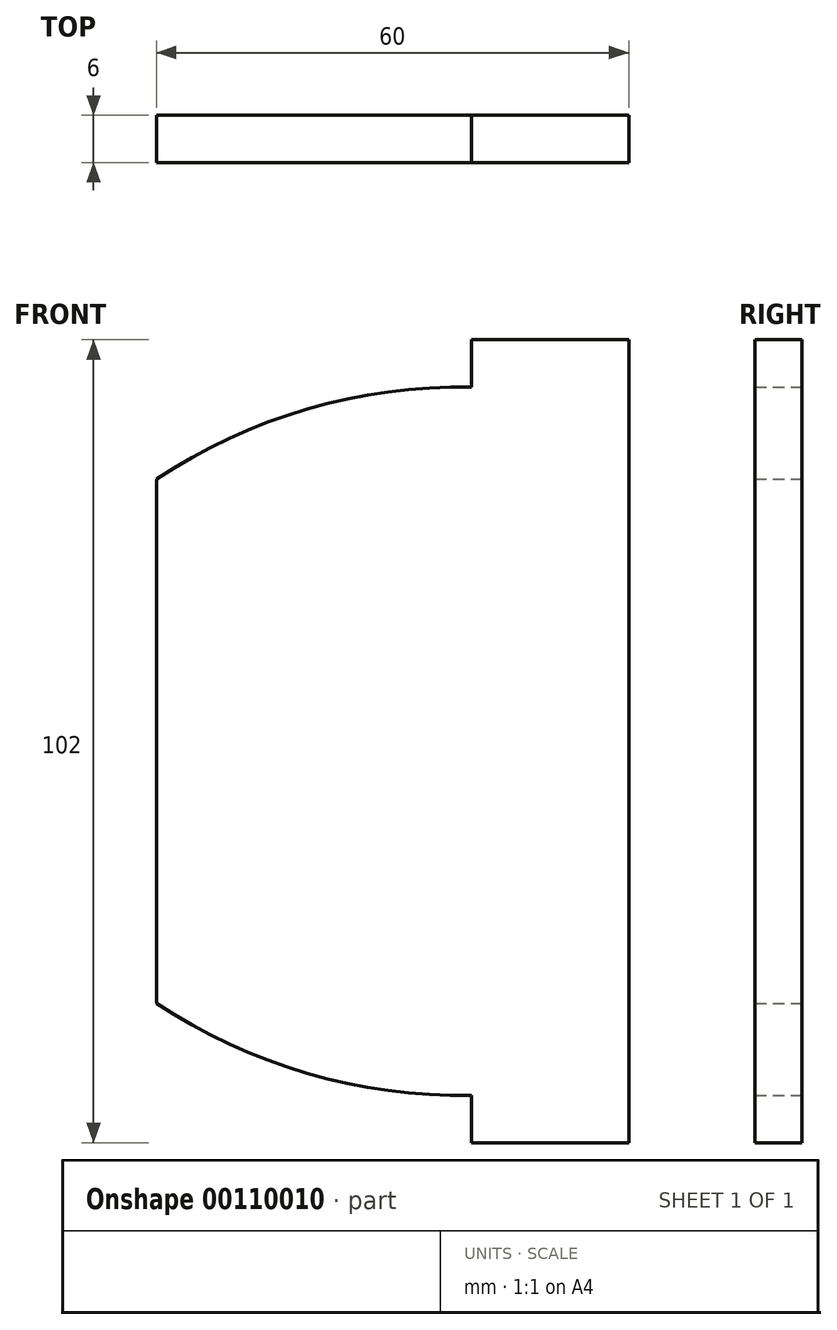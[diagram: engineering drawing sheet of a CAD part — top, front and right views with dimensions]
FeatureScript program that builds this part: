
annotation { "Feature Type Name" : "Feature", "Feature Type Description" : "" }
export const myFeature = defineFeature(function(context is Context, id is Id, definition is map)
    precondition{}
    {
        {
            var Q0;
            Q0=qCreatedBy(makeId("Front.planeOp"),FACE);
            var sketch = newSketch(context, id + "F0", { "sketchPlane" : qUnion([Q0])});
            skLineSegment(sketch, "E0.right", {"start": v(-45, -33.3) * mm, "end": v(-45, 33.3) * mm});
            skPoint(sketch, "E0.middle", {"position": v(0, 0) * mm});
            skLineSegment(sketch, "E1.top", {"start": v(-5, 51) * mm, "end": v(15, 51) * mm});
            skLineSegment(sketch, "E1.left", {"start": v(-5, 45) * mm, "end": v(-5, 51) * mm});
            skLineSegment(sketch, "E1.right", {"start": v(15, 45) * mm, "end": v(15, 51) * mm});
            skPoint(sketch, "E2.orphan", {"position": v(-45, 45) * mm});
            skArc(sketch, "E3", {"start": v(-5, 45) * mm, "mid": v(-25.89, 42.18) * mm, "end": v(-45, 33.3) * mm});
            skArc(sketch, "E4.MirrorCS", {"start": v(-5, -45) * mm, "mid": v(-25.89, -42.18) * mm, "end": v(-45, -33.3) * mm});
            skLineSegment(sketch, "E5.MirrorCS", {"start": v(-5, -45) * mm, "end": v(-5, -51) * mm});
            skLineSegment(sketch, "E6.MirrorCS", {"start": v(-5, -51) * mm, "end": v(15, -51) * mm});
            skLineSegment(sketch, "E7.MirrorCS", {"start": v(15, -45) * mm, "end": v(15, -51) * mm});
            skPoint(sketch, "E8.orphan", {"position": v(-45, -45) * mm});
            skLineSegment(sketch, "E9", {"start": v(15, 45) * mm, "end": v(15, -45) * mm});
            skPoint(sketch, "E0.left.end.orphan", {"position": v(45, 45) * mm});
            skPoint(sketch, "E0.left.start.orphan", {"position": v(45, -45) * mm});
            skSolve(sketch);
        }
        {
            var Q0;
            Q0 = qSketchRegion(id + "F0", true);
            extrude(context, id + "F1", {"entities" : qUnion([Q0]), "depth" : 6 * mm});
        }
    });
